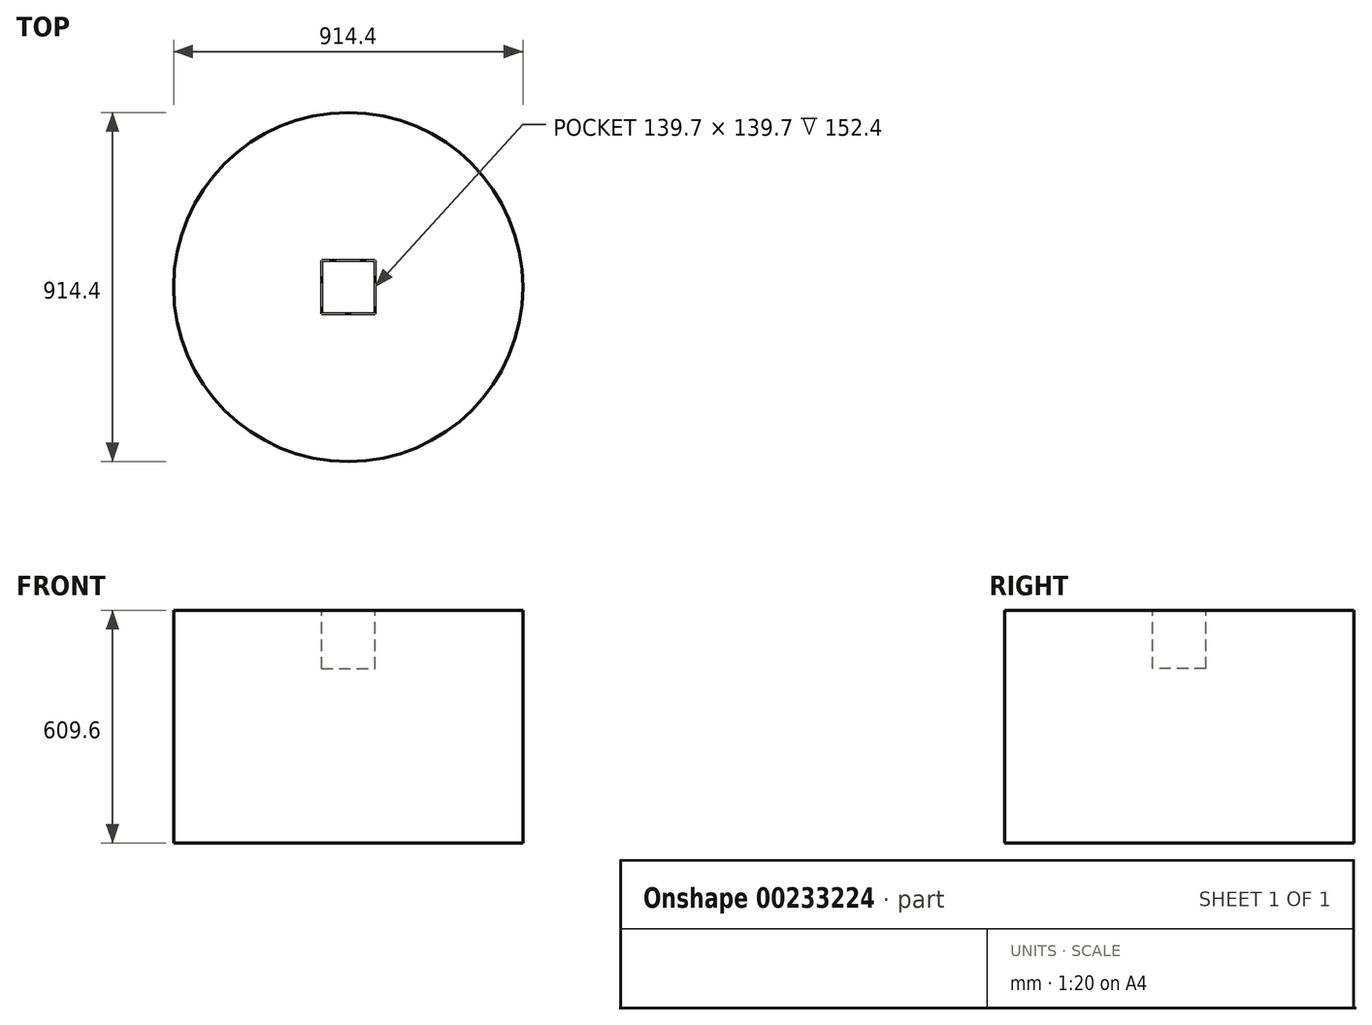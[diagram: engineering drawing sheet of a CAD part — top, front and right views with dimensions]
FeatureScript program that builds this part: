
annotation { "Feature Type Name" : "Feature", "Feature Type Description" : "" }
export const myFeature = defineFeature(function(context is Context, id is Id, definition is map)
    precondition{}
    {
        {
            var Q0;
            Q0=qCreatedBy(makeId("Top.planeOp"),FACE);
            var sketch = newSketch(context, id + "F0", { "sketchPlane" : qUnion([Q0])});
            skCircle(sketch, "E0", {"center": v(-108.95, -59.96) * mm, "radius": 457.2 * mm});
            skSolve(sketch);
        }
        {
            var Q0;
            Q0=makeQuery(id+"F0.imprint","IMPRINT",FACE,{"disambiguationData":[TD([[makeQuery(id+"F0.imprint","IMPRINT",EDGE,{"derivedFrom":sQuery(id+"F0.wireOp",EDGE,"E0")}),1.0]])]});
            extrude(context, id + "F1", {"entities" : qUnion([Q0]), "depth" : 609.6 * mm});
        }
        {
            var Q0;
            Q0=makeQuery(id+"F1.opExtrude","CAP_FACE",FACE,{"disambiguationData":[OSD([sQuery(id+"F0.wireOp",EDGE,"E0"),sQuery(id+"F0.wireOp",EDGE,"6P1Tywnk-tYaY-mJQP-wGXo-p6VKfE3N9jV0"),sQuery(id+"F0.wireOp",EDGE,"2a7hX22G-BEac-tVPd-9RZe-aDBDaKfjlETo"),sQuery(id+"F0.wireOp",EDGE,"MC2SpYfd-gGIS-zfzA-wTSh-PkraCtWPgqdu"),sQuery(id+"F0.wireOp",EDGE,"OwFIT4U5-2GGF-eI4M-DJ2x-qaRXkLKNF2s7")])],"isStart":false});
            var sketch = newSketch(context, id + "F2", { "sketchPlane" : qUnion([Q0])});
            skLineSegment(sketch, "E1.bottom", {"start": v(-178.8, 9.89) * mm, "end": v(-39.1, 9.89) * mm});
            skLineSegment(sketch, "E1.top", {"start": v(-178.8, -129.81) * mm, "end": v(-39.1, -129.81) * mm});
            skLineSegment(sketch, "E1.left", {"start": v(-178.8, 9.89) * mm, "end": v(-178.8, -129.81) * mm});
            skLineSegment(sketch, "E1.right", {"start": v(-39.1, 9.89) * mm, "end": v(-39.1, -129.81) * mm});
            skSolve(sketch);
        }
        {
            var Q0;
            Q0 = qSketchRegion(id + "F2", true);
            extrude(context, id + "F3", {"entities" : qUnion([Q0]), "operationType" : NewBodyOperationType.REMOVE, "oppositeDirection" : true, "depth" : 152.4 * mm});
        }
    });
